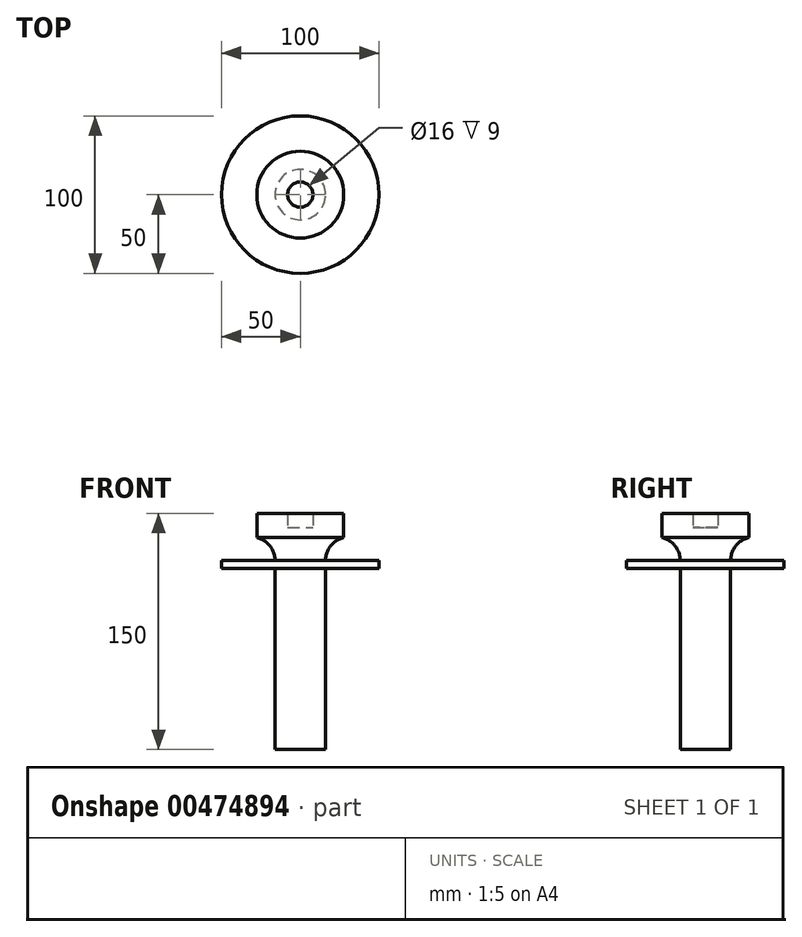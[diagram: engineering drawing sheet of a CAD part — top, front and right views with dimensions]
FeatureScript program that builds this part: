
annotation { "Feature Type Name" : "Feature", "Feature Type Description" : "" }
export const myFeature = defineFeature(function(context is Context, id is Id, definition is map)
    precondition{}
    {
        {
            var Q0;
            Q0=qCreatedBy(makeId("Front.planeOp"),FACE);
            var sketch = newSketch(context, id + "F0", { "sketchPlane" : qUnion([Q0])});
            skLineSegment(sketch, "E0.bottom", {"start": v(0, 0) * mm, "end": v(16, 0) * mm});
            skLineSegment(sketch, "E0.top", {"start": v(0, 141) * mm, "end": v(8, 141) * mm});
            skLineSegment(sketch, "E0.left", {"start": v(0, 0) * mm, "end": v(0, 141) * mm});
            skLineSegment(sketch, "E0.right", {"start": v(16, 0) * mm, "end": v(16, 115) * mm});
            skLineSegment(sketch, "E1.top", {"start": v(8, 150) * mm, "end": v(27.6, 150) * mm});
            skLineSegment(sketch, "E1.left", {"start": v(8, 141) * mm, "end": v(8, 150) * mm});
            skLineSegment(sketch, "E1.right", {"start": v(27.6, 134.6) * mm, "end": v(27.6, 150) * mm});
            skArc(sketch, "E2", {"start": v(27.6, 134.6) * mm, "mid": v(19.25, 129.33) * mm, "end": v(16, 120) * mm});
            skPoint(sketch, "E3.orphan", {"position": v(16, 141) * mm});
            skLineSegment(sketch, "E4", {"start": v(16, 120) * mm, "end": v(50, 120) * mm});
            skLineSegment(sketch, "E5", {"start": v(50, 120) * mm, "end": v(50, 115) * mm});
            skLineSegment(sketch, "E6", {"start": v(50, 115) * mm, "end": v(16, 115) * mm});
            skSolve(sketch);
        }
        {
            var Q0;
            Q0=makeQuery(id+"F0.imprint","IMPRINT",FACE,{"disambiguationData":[TD([[makeQuery(id+"F0.imprint","IMPRINT",EDGE,{"derivedFrom":sQuery(id+"F0.wireOp",EDGE,"E0.bottom")}),1.0]])]});
            var Q1;
            Q1=sQuery(id+"F0.wireOp",EDGE,"E0.left");
            revolve(context, id + "F1", {"entities" : qUnion([Q0]), "axis" : qUnion([Q1]), "revolveType" : RevolveType.FULL});
        }
    });
